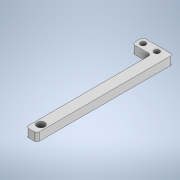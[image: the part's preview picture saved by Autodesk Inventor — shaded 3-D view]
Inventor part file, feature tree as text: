
AUTODESK INVENTOR PART (.ipt)
format: ipt  version: 2020 (Build 240168000, 168)  size: 271,360 bytes
history: native  units: mm
features: extrude x2, sketch x1, fillet x1
ambient origin geometry x8: Origin, YZ Plane, XZ Plane, XY Plane, X Axis, Y Axis, Z Axis, Center Point
bodies: Solide1 (feature_tree)
feature tree (4):
  sketch  "Esquisse1"
  extrude  "Extrusion1"  Depth=8.0mm
  fillet  "Congé1"  Radius=100.0mm
  extrude  "Extrusion2"  Depth=8.0mm
